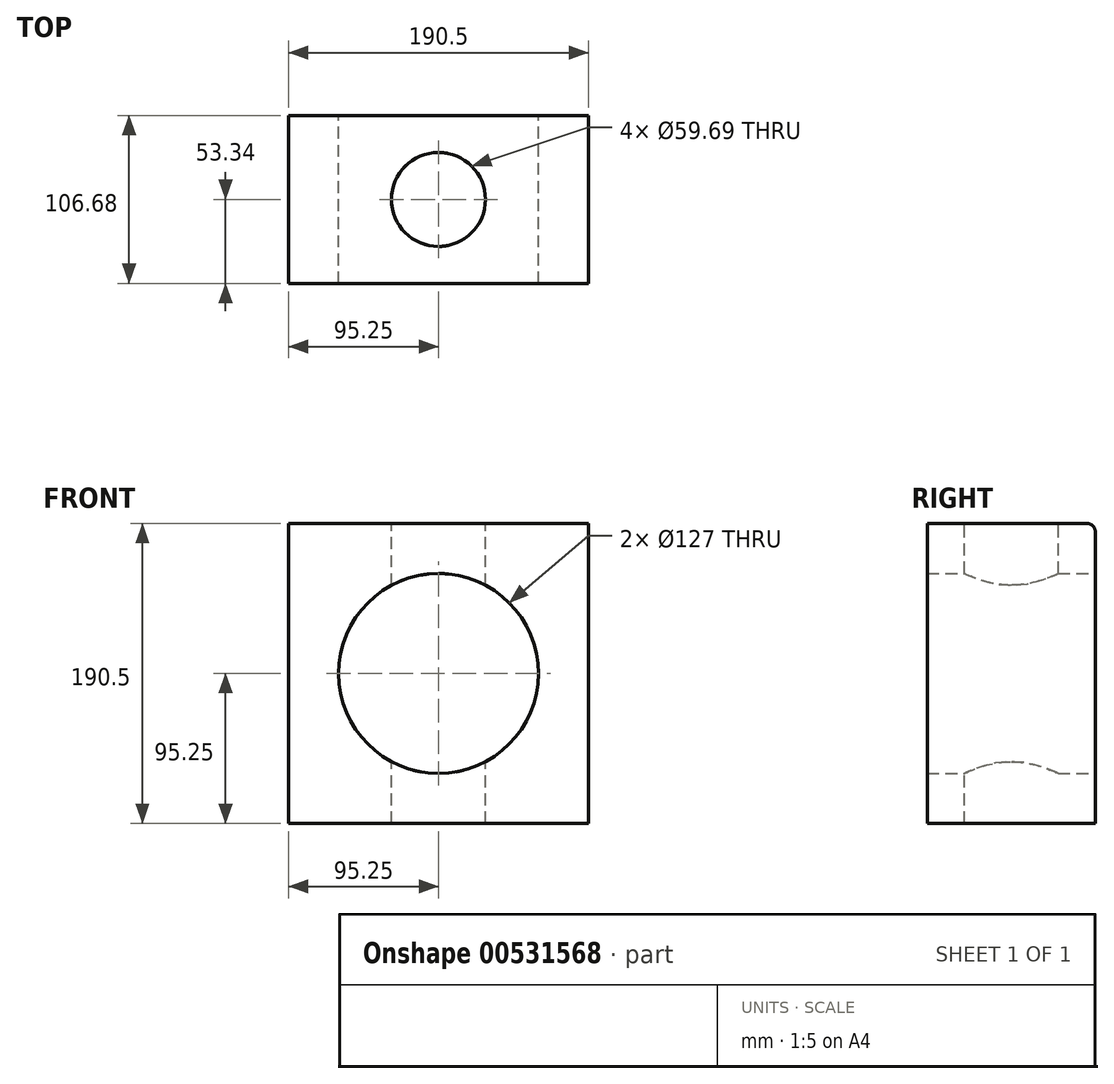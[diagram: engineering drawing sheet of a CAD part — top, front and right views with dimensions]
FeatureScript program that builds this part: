
annotation { "Feature Type Name" : "Feature", "Feature Type Description" : "" }
export const myFeature = defineFeature(function(context is Context, id is Id, definition is map)
    precondition{}
    {
        {
            var Q0;
            Q0=qCreatedBy(makeId("Front.planeOp"),FACE);
            var sketch = newSketch(context, id + "F0", { "sketchPlane" : qUnion([Q0])});
            skLineSegment(sketch, "E0.bottom", {"start": v(-127, -127) * mm, "end": v(127, -127) * mm});
            skLineSegment(sketch, "E0.top", {"start": v(-127, 127) * mm, "end": v(127, 127) * mm});
            skLineSegment(sketch, "E0.left", {"start": v(-127, -127) * mm, "end": v(-127, 127) * mm});
            skLineSegment(sketch, "E0.right", {"start": v(127, -127) * mm, "end": v(127, 127) * mm});
            skPoint(sketch, "E0.middle", {"position": v(0, 0) * mm});
            skLineSegment(sketch, "E1.bottom", {"start": v(-95.25, -95.25) * mm, "end": v(95.25, -95.25) * mm});
            skLineSegment(sketch, "E1.top", {"start": v(-95.25, 95.25) * mm, "end": v(95.25, 95.25) * mm});
            skLineSegment(sketch, "E1.left", {"start": v(-95.25, -95.25) * mm, "end": v(-95.25, 95.25) * mm});
            skLineSegment(sketch, "E1.right", {"start": v(95.25, -95.25) * mm, "end": v(95.25, 95.25) * mm});
            skCircle(sketch, "E2", {"center": v(0, 0) * mm, "radius": 63.5 * mm});
            skSolve(sketch);
        }
        {
            var Q0;
            Q0=makeQuery(id+"F0.imprint","IMPRINT",FACE,{"disambiguationData":[TD([[makeQuery(id+"F0.imprint","IMPRINT",EDGE,{"derivedFrom":sQuery(id+"F0.wireOp",EDGE,"E1.bottom")}),1.0]])]});
            extrude(context, id + "F1", {"entities" : qUnion([Q0]), "endBound" : BoundingType.SYMMETRIC, "depth" : 106.68 * mm, "offsetDistance" : 25.4 * mm});
        }
        {
            var Q0;
            Q0=makeQuery(id+"F1.opExtrude","SWEPT_FACE",FACE,{"disambiguationData":[OSD([sQuery(id+"F0.wireOp",EDGE,"E1.top")])]});
            var sketch = newSketch(context, id + "F2", { "sketchPlane" : qUnion([Q0])});
            skCircle(sketch, "E3", {"center": v(0, 0) * mm, "radius": 29.85 * mm});
            skSolve(sketch);
        }
        {
            var Q0;
            Q0=makeQuery(id+"F2.imprint","IMPRINT",FACE,{"disambiguationData":[TD([[makeQuery(id+"F2.imprint","IMPRINT",EDGE,{"derivedFrom":sQuery(id+"F2.wireOp",EDGE,"E3")}),1.0]])]});
            extrude(context, id + "F3", {"entities" : qUnion([Q0]), "operationType" : NewBodyOperationType.REMOVE, "endBound" : BoundingType.THROUGH_ALL, "oppositeDirection" : true, "depth" : 25.4 * mm, "offsetDistance" : 25.4 * mm});
        }
        {
            var Q0;
            Q0=makeQuery(id+"F3.boolean.opBoolean","COPY",EDGE,{"derivedFrom":makeQuery(id+"F3.opExtrude","CAP_EDGE",EDGE,{"disambiguationData":[OSD([sQuery(id+"F2.wireOp",EDGE,"E3")])],"isStart":true})});
            var Q1;
            Q1=makeQuery(id+"F1.opExtrude","CAP_EDGE",EDGE,{"disambiguationData":[OSD([sQuery(id+"F0.wireOp",EDGE,"E1.top")])],"isStart":true});
            fillet(context, id + "F4", {"entities" : qUnion([Q0, Q1]), "radius" : 5.08 * mm, "tangentPropagation" : true, "allowEdgeOverflow" : false});
        }
    });
